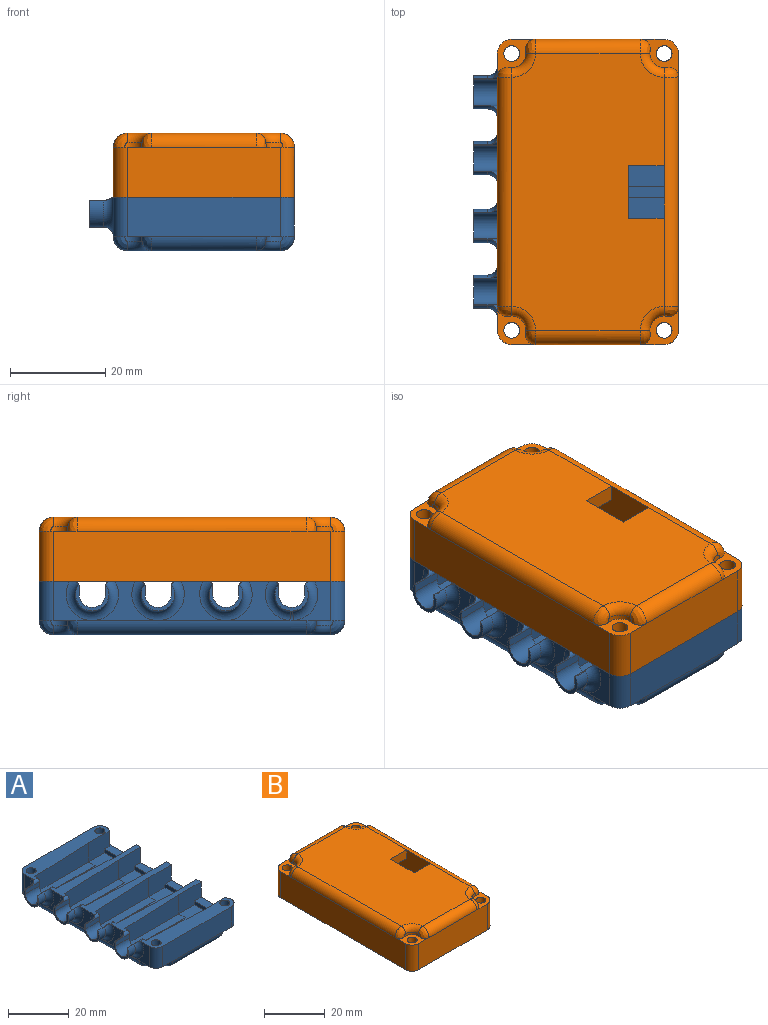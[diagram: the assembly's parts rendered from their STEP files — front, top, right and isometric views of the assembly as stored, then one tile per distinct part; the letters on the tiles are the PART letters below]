
ASSEMBLY  parts=2 mates=1
PART A: 134 faces, bbox 43.1x64.2x13.3 mm
  f0: plane 58.07x32mm, normal (0,0,-1), area 1779.6mm2, adj f87,f88,f89,f90,f123,f126,f129,f132
  f1: plane 8.2x7.75mm, normal (-1,0,0), area 28.5mm2, adj f85,f87,f99,f112,f121
  f2: plane 41.47x8.2mm, normal (-1,0,0), area 115.3mm2, adj f87,f101,f102,f103,f104,f118,f119,f120
  f3: plane 8.2x8.11mm, normal (-1,0,0), area 28.5mm2, adj f84,f87,f104,f110,f117
  f4: cylinder r=2.75mm len=6.5mm, axis (1,0,0), area 56.2mm2, adj f5,f21,f22,f98
  f5: plane 9.77x7.7mm, normal (1,0,0), area 48.1mm2, adj f4,f6,f13,f14,f21,f22,f81,f82
  f6: plane 33.5x11.85mm, normal (0,0,1), area 219.8mm2, adj f5,f7,f8,f11,f13,f14,f15,f16
  f7: plane 9.55x7.7mm, normal (0,1,0), area 70.5mm2, adj f6,f11,f12,f13,f86,f121
  f8: plane 10.5x7.7mm, normal (0,-1,0), area 76.3mm2, adj f6,f9,f11,f12,f14,f120
  f9: plane 58.07x8.2mm, normal (1,0,0), area 155.2mm2, adj f8,f12,f26,f27,f29,f44,f47,f61
  f10: plane 32x8.2mm, normal (0,-1,0), area 262.4mm2, adj f85,f86,f88,f108,f112,f121
  f11: plane 11.85x1.5mm, normal (-1,0,0), area 17.8mm2, adj f6,f7,f8,f12
  f12: plane 14.03x3mm, normal (0,0,1), area 36.2mm2, adj f7,f8,f9,f11,f86
  f13: plane 26x7.7mm, normal (0.04,1,0), area 187.9mm2, adj f5,f6,f7,f18,f19,f121
  f14: plane 26x7.7mm, normal (0.04,-1,0), area 187.9mm2, adj f5,f6,f8,f15,f16,f120
  f15: plane 25.12x4mm, normal (0.04,0,1), area 75.1mm2, adj f6,f14,f16,f17
  f16: plane 3x1mm, normal (-1,-0.04,0), area 3mm2, adj f6,f14,f15,f17
  f17: plane 25x1mm, normal (0.04,-1,0), area 12.5mm2, adj f6,f15,f16
  f18: plane 25.12x4mm, normal (0.04,0,1), area 75.1mm2, adj f6,f13,f19,f20
  f19: plane 3x1mm, normal (-1,0.04,0), area 3mm2, adj f6,f13,f18,f20
  f20: plane 25x1mm, normal (0.04,1,0), area 12.5mm2, adj f6,f18,f19
  f21: plane 6.5x1.72mm, normal (0,1,0), area 11.2mm2, adj f4,f5,f82,f98
  f22: plane 6.5x1.69mm, normal (0,-1,0), area 11mm2, adj f4,f5,f81,f98
  f23: cylinder r=2.75mm len=6.5mm, axis (1,0,0), area 56.2mm2, adj f24,f38,f39,f96
  f24: plane 9.77x7.7mm, normal (1,0,0), area 48.1mm2, adj f23,f25,f30,f31,f38,f39,f79,f80
  f25: plane 33.5x11.85mm, normal (0,0,1), area 219.8mm2, adj f24,f26,f27,f28,f30,f31,f32,f33
  f26: plane 10.5x7.7mm, normal (0,-1,0), area 76.3mm2, adj f9,f25,f28,f29,f30,f119
  f27: plane 10.5x7.7mm, normal (0,1,0), area 76.3mm2, adj f9,f25,f28,f29,f31,f120
  f28: plane 11.85x1.5mm, normal (-1,0,0), area 17.8mm2, adj f25,f26,f27,f29
  f29: plane 11.85x3mm, normal (0,0,1), area 35.6mm2, adj f9,f26,f27,f28
  f30: plane 26x7.7mm, normal (0.04,-1,0), area 187.9mm2, adj f24,f25,f26,f35,f36,f119
  f31: plane 26x7.7mm, normal (0.04,1,0), area 187.9mm2, adj f24,f25,f27,f32,f33,f120
  f32: plane 25.12x4mm, normal (0.04,0,1), area 75.1mm2, adj f25,f31,f33,f34
  f33: plane 3x1mm, normal (-1,0.04,0), area 3mm2, adj f25,f31,f32,f34
  f34: plane 25x1mm, normal (0.04,1,0), area 12.5mm2, adj f25,f32,f33
  f35: plane 25.12x4mm, normal (0.04,0,1), area 75.1mm2, adj f25,f30,f36,f37
  f36: plane 3x1mm, normal (-1,-0.04,0), area 3mm2, adj f25,f30,f35,f37
  f37: plane 25x1mm, normal (0.04,-1,0), area 12.5mm2, adj f25,f35,f36
  f38: plane 6.5x1.72mm, normal (0,-1,0), area 11.2mm2, adj f23,f24,f79,f96
  f39: plane 6.5x1.69mm, normal (0,1,0), area 11mm2, adj f23,f24,f80,f96
  f40: cylinder r=2.75mm len=6.5mm, axis (1,0,0), area 56.2mm2, adj f41,f56,f57,f92
  f41: plane 9.77x7.7mm, normal (1,0,0), area 48.1mm2, adj f40,f42,f48,f49,f56,f57,f76,f78
  f42: plane 33.5x11.85mm, normal (0,0,1), area 219.8mm2, adj f41,f43,f44,f46,f48,f49,f50,f51
  f43: plane 9.55x7.7mm, normal (0,-1,0), area 70.5mm2, adj f42,f46,f47,f48,f83,f117
  f44: plane 10.5x7.7mm, normal (0,1,0), area 76.3mm2, adj f9,f42,f46,f47,f49,f118
  f45: plane 32x8.2mm, normal (0,1,0), area 262.4mm2, adj f83,f84,f89,f106,f110,f117
  f46: plane 11.85x1.5mm, normal (-1,0,0), area 17.8mm2, adj f42,f43,f44,f47
  f47: plane 14.03x3mm, normal (0,0,1), area 36.2mm2, adj f9,f43,f44,f46,f83
  f48: plane 26x7.7mm, normal (0.04,-1,0), area 187.9mm2, adj f41,f42,f43,f53,f54,f117
  f49: plane 26x7.7mm, normal (0.04,1,0), area 187.9mm2, adj f41,f42,f44,f50,f51,f118
  f50: plane 25.12x4mm, normal (0.04,0,1), area 75.1mm2, adj f42,f49,f51,f52
  f51: plane 3x1mm, normal (-1,0.04,0), area 3mm2, adj f42,f49,f50,f52
  f52: plane 25x1mm, normal (0.04,1,0), area 12.5mm2, adj f42,f50,f51
  f53: plane 25.12x4mm, normal (0.04,0,1), area 75.1mm2, adj f42,f48,f54,f55
  f54: plane 3x1mm, normal (-1,-0.04,0), area 3mm2, adj f42,f48,f53,f55
  f55: plane 25x1mm, normal (0.04,-1,0), area 12.5mm2, adj f42,f53,f54
  f56: plane 6.5x1.72mm, normal (0,-1,0), area 11.2mm2, adj f40,f41,f76,f92
  f57: plane 6.5x1.69mm, normal (0,1,0), area 11mm2, adj f40,f41,f78,f92
  f58: cylinder r=2.75mm len=6.5mm, axis (1,0,0), area 56.2mm2, adj f59,f73,f74,f94
  f59: plane 9.77x7.7mm, normal (1,0,0), area 48.1mm2, adj f58,f60,f65,f66,f73,f74,f75,f77
  f60: plane 33.5x11.85mm, normal (0,0,1), area 219.8mm2, adj f59,f61,f62,f63,f65,f66,f67,f68
  f61: plane 10.5x7.7mm, normal (0,1,0), area 76.3mm2, adj f9,f60,f63,f64,f65,f119
  f62: plane 10.5x7.7mm, normal (0,-1,0), area 76.3mm2, adj f9,f60,f63,f64,f66,f118
  f63: plane 11.85x1.5mm, normal (-1,0,0), area 17.8mm2, adj f60,f61,f62,f64
  f64: plane 11.85x3mm, normal (0,0,1), area 35.6mm2, adj f9,f61,f62,f63
  f65: plane 26x7.7mm, normal (0.04,1,0), area 187.9mm2, adj f59,f60,f61,f70,f71,f119
  f66: plane 26x7.7mm, normal (0.04,-1,0), area 187.9mm2, adj f59,f60,f62,f67,f68,f118
  f67: plane 25.12x4mm, normal (0.04,0,1), area 75.1mm2, adj f60,f66,f68,f69
  f68: plane 3x1mm, normal (-1,-0.04,0), area 3mm2, adj f60,f66,f67,f69
  f69: plane 25x1mm, normal (0.04,-1,0), area 12.5mm2, adj f60,f67,f68
  f70: plane 25.12x4mm, normal (0.04,0,1), area 75.1mm2, adj f60,f65,f71,f72
  f71: plane 3x1mm, normal (-1,0.04,0), area 3mm2, adj f60,f65,f70,f72
  f72: plane 25x1mm, normal (0.04,1,0), area 12.5mm2, adj f60,f70,f71
  f73: plane 6.5x1.72mm, normal (0,1,0), area 11.2mm2, adj f58,f59,f75,f94
  f74: plane 6.5x1.69mm, normal (0,-1,0), area 11mm2, adj f58,f59,f77,f94
  f75: cylinder r=1mm len=6.5mm, axis (1,0,0), area 5mm2, adj f59,f73,f93,f94,f103,f119
  f76: cylinder r=1mm len=6.5mm, axis (1,0,0), area 5mm2, adj f41,f56,f91,f92,f104,f117
  f77: cylinder r=1mm len=6.5mm, axis (-1,0,0), area 5.2mm2, adj f59,f74,f93,f94,f103,f118
  f78: cylinder r=1mm len=6.5mm, axis (-1,0,0), area 5.1mm2, adj f41,f57,f91,f92,f104,f118
  f79: cylinder r=1mm len=6.5mm, axis (1,0,0), area 5mm2, adj f24,f38,f95,f96,f102,f119
  f80: cylinder r=1mm len=6.5mm, axis (-1,0,0), area 5.2mm2, adj f24,f39,f95,f96,f102,f120
  f81: cylinder r=1mm len=6.5mm, axis (-1,0,0), area 5.1mm2, adj f5,f22,f97,f98,f101,f120
  f82: cylinder r=1mm len=6.5mm, axis (1,0,0), area 4.9mm2, adj f5,f21,f97,f98,f99,f121
  f83: cylinder r=3mm len=8.2mm, axis (0,0,-1), area 53.8mm2, adj f9,f43,f45,f47,f106,f117
  f84: cylinder r=3mm len=8.2mm, axis (0,0,-1), area 38.6mm2, adj f3,f45,f110,f117
  f85: cylinder r=3mm len=8.2mm, axis (0,0,-1), area 38.6mm2, adj f1,f10,f112,f121
  f86: cylinder r=3mm len=8.2mm, axis (0,0,-1), area 53.8mm2, adj f7,f9,f10,f12,f108,f121
  f87: cylinder r=3mm len=48.27mm, axis (0,-1,0), area 227mm2, adj f0,f1,f2,f3,f100,f124,f125
  f88: cylinder r=3mm len=22.2mm, axis (1,0,0), area 104.1mm2, adj f0,f10,f122,f128
  f89: cylinder r=3mm len=22.2mm, axis (1,0,0), area 104.1mm2, adj f0,f45,f127,f133
  f90: cylinder r=3mm len=48.27mm, axis (0,1,0), area 227mm2, adj f0,f9,f130,f131
  f91: cylinder r=3.5mm len=7mm, axis (1,0,0), area 46.3mm2, adj f76,f78,f92,f104
  f92: plane 7x5.57mm, normal (-1,0,0), area 9.5mm2, adj f40,f56,f57,f76,f78,f91
  f93: cylinder r=3.5mm len=7mm, axis (1,0,0), area 46.2mm2, adj f75,f77,f94,f103
  f94: plane 7x5.58mm, normal (-1,0,0), area 9.5mm2, adj f58,f73,f74,f75,f77,f93
  f95: cylinder r=3.5mm len=7mm, axis (1,0,0), area 46.2mm2, adj f79,f80,f96,f102
  f96: plane 7x5.58mm, normal (-1,0,0), area 9.5mm2, adj f23,f38,f39,f79,f80,f95
  f97: cylinder r=3.5mm len=7mm, axis (1,0,0), area 46.3mm2, adj f81,f82,f98,f99,f100,f101
  f98: plane 7x5.59mm, normal (-1,0,0), area 9.6mm2, adj f4,f21,f22,f81,f82,f97
  f99: torus R=5.5mm, axis (-1,0,0), area 28.2mm2, adj f1,f82,f97,f100,f121
  f100: bspline ~3.15x2.14mm, area 1.8mm2, adj f87,f97,f99,f101
  f101: torus R=5.5mm, axis (-1,0,0), area 28.3mm2, adj f2,f81,f97,f100,f120
  f102: torus R=5.5mm, axis (-1,0,0), area 58.2mm2, adj f2,f79,f80,f95,f119,f120
  f103: torus R=5.5mm, axis (-1,0,0), area 58.2mm2, adj f2,f75,f77,f93,f118,f119
  f104: torus R=5.5mm, axis (-1,0,0), area 58.3mm2, adj f2,f3,f76,f78,f91,f117,f118
  f105: cylinder r=3mm len=3.6mm, axis (0,0,-1), area 5.7mm2, adj f106,f131,f132,f133
  f106: plane 7.99x7.99mm, normal (0,0,-1), area 24.8mm2, adj f9,f45,f83,f105,f116,f131,f133
  f107: cylinder r=3mm len=3.6mm, axis (0,0,-1), area 5.7mm2, adj f108,f128,f129,f130
  f108: plane 7.99x7.99mm, normal (0,0,-1), area 24.8mm2, adj f9,f10,f86,f107,f114,f128,f130
  f109: cylinder r=3mm len=3.6mm, axis (0,0,-1), area 5.7mm2, adj f110,f125,f126,f127
  f110: plane 7.99x7.99mm, normal (0,0,-1), area 24.8mm2, adj f3,f45,f84,f109,f115,f125,f127
  f111: cylinder r=3mm len=3.6mm, axis (0,0,-1), area 5.7mm2, adj f112,f122,f123,f124
  f112: plane 7.99x7.99mm, normal (0,0,-1), area 24.8mm2, adj f1,f10,f85,f111,f113,f122,f124
  f113: cylinder r=1.65mm len=8.2mm, axis (0,0,-1), area 85mm2, adj f112,f121
  f114: cylinder r=1.65mm len=8.2mm, axis (0,0,-1), area 85mm2, adj f108,f121
  f115: cylinder r=1.65mm len=8.2mm, axis (0,0,-1), area 85mm2, adj f110,f117
  f116: cylinder r=1.65mm len=8.2mm, axis (0,0,-1), area 85mm2, adj f106,f117
  f117: plane 38.24x7.39mm, normal (0,0,1), area 192.2mm2, adj f3,f41,f43,f45,f48,f76,f83,f84
  f118: plane 38.25x6.36mm, normal (0,0,1), area 108.5mm2, adj f2,f9,f41,f44,f49,f59,f62,f66
  f119: plane 38.24x6.74mm, normal (0,0,1), area 123.6mm2, adj f2,f9,f24,f26,f30,f59,f61,f65
  f120: plane 38.25x6.36mm, normal (0,0,1), area 108.5mm2, adj f2,f5,f8,f9,f14,f24,f27,f31
  f121: plane 38.23x7.39mm, normal (0,0,1), area 192.2mm2, adj f1,f5,f7,f10,f13,f82,f85,f86
  f122: bspline ~3.56x3.51mm, area 11.5mm2, adj f88,f111,f112,f123
  f123: torus R=5mm, axis (0,0,1), area 18.4mm2, adj f0,f111,f122,f124
  f124: bspline ~3.56x3.51mm, area 11.5mm2, adj f87,f111,f112,f123
  f125: bspline ~3.56x3.51mm, area 11.5mm2, adj f87,f109,f110,f126
  f126: torus R=5mm, axis (0,0,1), area 18.4mm2, adj f0,f109,f125,f127
  f127: bspline ~3.56x3.51mm, area 11.5mm2, adj f89,f109,f110,f126
  f128: bspline ~3.56x3.51mm, area 11.5mm2, adj f88,f107,f108,f129
  f129: torus R=5mm, axis (0,0,1), area 18.4mm2, adj f0,f107,f128,f130
  f130: bspline ~3.56x3.51mm, area 11.5mm2, adj f90,f107,f108,f129
  f131: bspline ~3.56x3.51mm, area 11.5mm2, adj f90,f105,f106,f132
  f132: torus R=5mm, axis (0,0,1), area 18.4mm2, adj f0,f105,f131,f133
  f133: bspline ~3.56x3.51mm, area 11.5mm2, adj f89,f105,f106,f132
PART B: 115 faces, bbox 38.1x64.2x13.6 mm
  f0: plane 21.35x7.51mm, normal (0,0,-1), area 160.4mm2, adj f5,f62,f79,f113
  f1: plane 58.07x32mm, normal (0,0,1), area 1697.2mm2, adj f2,f35,f36,f47,f79,f86,f89,f96
  f2: cylinder r=3mm len=48.27mm, axis (0,1,0), area 226.8mm2, adj f1,f4,f5,f85,f98,f113,f114
  f3: plane 3.93x2.98mm, normal (0,0,-1), area 11.7mm2, adj f4,f5,f23,f110
  f4: plane 58.07x10.5mm, normal (1,0,0), area 503.8mm2, adj f2,f3,f6,f7,f8,f14,f15,f16
  f5: plane 53.7x13.5mm, normal (-1,0,0), area 471.8mm2, adj f0,f2,f3,f6,f7,f8,f14,f15
  f6: plane 3.93x2.98mm, normal (0,0,-1), area 11.7mm2, adj f4,f5,f21,f107
  f7: plane 3.93x2.98mm, normal (0,0,-1), area 11.7mm2, adj f4,f5,f20,f104
  f8: plane 6.11x2.98mm, normal (0,0,-1), area 12.3mm2, adj f4,f5,f59,f62,f101
  f9: cylinder r=3mm len=10.5mm, axis (0,0,-1), area 49.5mm2, adj f60,f77,f78,f91
  f10: cylinder r=1.65mm len=10.5mm, axis (0,0,-1), area 108.9mm2, adj f78,f93
  f11: cylinder r=1.65mm len=10.5mm, axis (0,0,-1), area 108.9mm2, adj f78,f91
  f12: cylinder r=1.65mm len=10.5mm, axis (0,0,-1), area 108.9mm2, adj f78,f83
  f13: cylinder r=1.65mm len=10.5mm, axis (0,0,-1), area 108.9mm2, adj f78,f81
  f14: plane 3.93x2.98mm, normal (0,0,-1), area 11.7mm2, adj f4,f5,f19,f105
  f15: plane 3.93x2.98mm, normal (0,0,-1), area 11.7mm2, adj f4,f5,f22,f108
  f16: plane 6.11x2.98mm, normal (0,0,-1), area 12.3mm2, adj f4,f5,f72,f74,f111
  f17: plane 3.93x2.98mm, normal (0,0,-1), area 11.7mm2, adj f4,f5,f18,f102
  f18: plane 2.98x0.5mm, normal (0,-1,0), area 1.5mm2, adj f4,f5,f17,f24
  f19: plane 2.98x0.5mm, normal (0,-1,0), area 1.5mm2, adj f4,f5,f14,f25
  f20: plane 2.98x0.5mm, normal (0,1,0), area 1.5mm2, adj f4,f5,f7,f24
  f21: plane 2.98x0.5mm, normal (0,-1,0), area 1.5mm2, adj f4,f5,f6,f26
  f22: plane 2.98x0.5mm, normal (0,1,0), area 1.5mm2, adj f4,f5,f15,f25
  f23: plane 2.98x0.5mm, normal (0,1,0), area 1.5mm2, adj f3,f4,f5,f26
  f24: plane 2.98x1.97mm, normal (0,0,-1), area 5.9mm2, adj f4,f5,f18,f20
  f25: plane 2.98x2.37mm, normal (0,0,-1), area 7.1mm2, adj f4,f5,f19,f22
  f26: plane 2.98x1.97mm, normal (0,0,-1), area 5.9mm2, adj f4,f5,f21,f23
  f27: plane 24.88x1mm, normal (0.04,1,0), area 12.5mm2, adj f37,f38,f39,f79
  f28: plane 24.88x1mm, normal (0.04,-1,0), area 12.5mm2, adj f39,f40,f41,f79
  f29: plane 24.88x1mm, normal (0.04,1,0), area 12.5mm2, adj f44,f45,f46,f79
  f30: plane 24.88x1mm, normal (0.04,-1,0), area 12.5mm2, adj f42,f43,f46,f79
  f31: plane 24.88x1mm, normal (0.04,1,0), area 12.5mm2, adj f50,f51,f52,f79
  f32: plane 24.88x1mm, normal (0.04,-1,0), area 12.5mm2, adj f48,f49,f52,f79
  f33: plane 24.88x1mm, normal (0.04,1,0), area 12.5mm2, adj f53,f54,f55,f79
  f34: plane 24.88x1mm, normal (0.04,-1,0), area 12.5mm2, adj f55,f56,f57,f79
  f35: cylinder r=3mm len=48.27mm, axis (0,-1,0), area 227mm2, adj f1,f77,f90,f95
  f36: cylinder r=3mm len=22.2mm, axis (1,0,0), area 104.1mm2, adj f1,f60,f97,f100
  f37: plane 25x4mm, normal (0.04,0,-1), area 74.9mm2, adj f27,f38,f61,f79
  f38: plane 3x1mm, normal (-1,0.04,0), area 3mm2, adj f27,f37,f39,f61
  f39: plane 26x9.85mm, normal (0,0,-1), area 131.3mm2, adj f27,f28,f38,f40,f58,f61,f63,f79
  f40: plane 3x1mm, normal (-1,-0.04,0), area 3mm2, adj f28,f39,f41,f58
  f41: plane 25x4mm, normal (0.04,0,-1), area 74.9mm2, adj f28,f40,f58,f79
  f42: plane 3x1mm, normal (-1,-0.04,0), area 3mm2, adj f30,f43,f46,f64
  f43: plane 25x4mm, normal (0.04,0,-1), area 74.9mm2, adj f30,f42,f64,f79
  f44: plane 25x4mm, normal (0.04,0,-1), area 74.9mm2, adj f29,f45,f65,f79
  f45: plane 3x1mm, normal (-1,0.04,0), area 3mm2, adj f29,f44,f46,f65
  f46: plane 26x9.85mm, normal (0,0,-1), area 131.3mm2, adj f29,f30,f42,f45,f64,f65,f66,f79
  f47: cylinder r=3mm len=22.2mm, axis (1,0,0), area 104.1mm2, adj f1,f73,f87,f88
  f48: plane 3x1mm, normal (-1,-0.04,0), area 3mm2, adj f32,f49,f52,f70
  f49: plane 25x4mm, normal (0.04,0,-1), area 74.9mm2, adj f32,f48,f70,f79
  f50: plane 25x4mm, normal (0.04,0,-1), area 74.9mm2, adj f31,f51,f75,f79
  f51: plane 3x1mm, normal (-1,0.04,0), area 3mm2, adj f31,f50,f52,f75
  f52: plane 26x9.85mm, normal (0,0,-1), area 131.3mm2, adj f31,f32,f48,f51,f70,f75,f76,f79
  f53: plane 25x4mm, normal (0.04,0,-1), area 74.9mm2, adj f33,f54,f68,f79
  f54: plane 3x1mm, normal (-1,0.04,0), area 3mm2, adj f33,f53,f55,f68
  f55: plane 26x9.85mm, normal (0,0,-1), area 131.3mm2, adj f33,f34,f54,f56,f67,f68,f69,f79
  f56: plane 3x1mm, normal (-1,-0.04,0), area 3mm2, adj f34,f55,f57,f67
  f57: plane 25x4mm, normal (0.04,0,-1), area 74.9mm2, adj f34,f56,f67,f79
  f58: plane 26x2mm, normal (0.04,-1,0), area 39.5mm2, adj f39,f40,f41,f63,f78,f79
  f59: cylinder r=3mm len=10.5mm, axis (0,0,-1), area 50.7mm2, adj f4,f8,f60,f62,f78,f93
  f60: plane 32x10.5mm, normal (0,-1,0), area 336mm2, adj f9,f36,f59,f78,f91,f93
  f61: plane 26x2mm, normal (0.04,1,0), area 39.5mm2, adj f37,f38,f39,f62,f63,f78
  f62: plane 10x9.55mm, normal (0,1,0), area 76.2mm2, adj f0,f5,f8,f59,f61,f78,f79
  f63: plane 9.77x2mm, normal (1,0,0), area 19.5mm2, adj f39,f58,f61,f78
  f64: plane 26x2mm, normal (0.04,-1,0), area 39.5mm2, adj f42,f43,f46,f66,f78,f79
  f65: plane 26x2mm, normal (0.04,1,0), area 39.5mm2, adj f44,f45,f46,f66,f78,f79
  f66: plane 9.77x2mm, normal (1,0,0), area 19.5mm2, adj f46,f64,f65,f78
  f67: plane 26x2mm, normal (0.04,-1,0), area 39.5mm2, adj f55,f56,f57,f69,f78,f79
  f68: plane 26x2mm, normal (0.04,1,0), area 39.5mm2, adj f53,f54,f55,f69,f78,f79
  f69: plane 9.77x2mm, normal (1,0,0), area 19.5mm2, adj f55,f67,f68,f78
  f70: plane 26x2mm, normal (0.04,-1,0), area 39.5mm2, adj f48,f49,f52,f74,f76,f78
  f71: cylinder r=3mm len=10.5mm, axis (0,0,-1), area 49.5mm2, adj f73,f77,f78,f81
  f72: cylinder r=3mm len=10.5mm, axis (0,0,-1), area 50.7mm2, adj f4,f16,f73,f74,f78,f83
  f73: plane 32x10.5mm, normal (0,1,0), area 336mm2, adj f47,f71,f72,f78,f81,f83
  f74: plane 10x9.55mm, normal (0,-1,0), area 76.2mm2, adj f5,f16,f70,f72,f78,f79,f80
  f75: plane 26x2mm, normal (0.04,1,0), area 39.5mm2, adj f50,f51,f52,f76,f78,f79
  f76: plane 9.77x2mm, normal (1,0,0), area 19.5mm2, adj f52,f70,f75,f78
  f77: plane 58.08x10.52mm, normal (-1,0,0), area 609.7mm2, adj f9,f35,f71,f78,f81,f91
  f78: plane 64.07x38mm, normal (0,0,-1), area 703.3mm2, adj f9,f10,f11,f12,f13,f58,f59,f60
  f79: plane 53.7x13.5mm, normal (1,0,0), area 480.8mm2, adj f0,f1,f27,f28,f29,f30,f31,f32
  f80: plane 21.35x7.51mm, normal (0,0,-1), area 160.4mm2, adj f5,f74,f79,f114
  f81: plane 7.99x7.99mm, normal (0,0,1), area 24.8mm2, adj f13,f71,f73,f77,f82,f88,f90
  f82: cylinder r=3mm len=3.6mm, axis (0,0,1), area 5.7mm2, adj f81,f88,f89,f90
  f83: plane 7.99x7.99mm, normal (0,0,1), area 24.8mm2, adj f4,f12,f72,f73,f84,f85,f87
  f84: cylinder r=3mm len=3.6mm, axis (0,0,1), area 5.7mm2, adj f83,f85,f86,f87
  f85: bspline ~3.56x3.51mm, area 11.5mm2, adj f2,f83,f84,f86
  f86: torus R=5mm, axis (0,0,-1), area 18.4mm2, adj f1,f84,f85,f87
  f87: bspline ~3.56x3.51mm, area 11.5mm2, adj f47,f83,f84,f86
  f88: bspline ~3.56x3.51mm, area 11.5mm2, adj f47,f81,f82,f89
  f89: torus R=5mm, axis (0,0,-1), area 18.4mm2, adj f1,f82,f88,f90
  f90: bspline ~3.56x3.51mm, area 11.5mm2, adj f35,f81,f82,f89
  f91: plane 7.99x7.99mm, normal (0,0,1), area 24.8mm2, adj f9,f11,f60,f77,f92,f95,f97
  f92: cylinder r=3mm len=3.6mm, axis (0,0,1), area 5.7mm2, adj f91,f95,f96,f97
  f93: plane 7.99x7.99mm, normal (0,0,1), area 24.8mm2, adj f4,f10,f59,f60,f94,f98,f100
  f94: cylinder r=3mm len=3.6mm, axis (0,0,1), area 5.7mm2, adj f93,f98,f99,f100
  f95: bspline ~3.56x3.51mm, area 11.5mm2, adj f35,f91,f92,f96
  f96: torus R=5mm, axis (0,0,-1), area 18.4mm2, adj f1,f92,f95,f97
  f97: bspline ~3.56x3.51mm, area 11.5mm2, adj f36,f91,f92,f96
  f98: bspline ~3.56x3.51mm, area 11.5mm2, adj f2,f93,f94,f99
  f99: torus R=5mm, axis (0,0,-1), area 18.4mm2, adj f1,f94,f98,f100
  f100: bspline ~3.56x3.51mm, area 11.5mm2, adj f36,f93,f94,f99
  f101: plane 5x2.98mm, normal (0,1,0), area 14.9mm2, adj f4,f5,f8,f103
  f102: plane 5x2.98mm, normal (0,-1,0), area 14.9mm2, adj f4,f5,f17,f103
  f103: plane 4x2.98mm, normal (0,0,-1), area 11.9mm2, adj f4,f5,f101,f102
  f104: plane 5x2.98mm, normal (0,1,0), area 14.9mm2, adj f4,f5,f7,f106
  f105: plane 5x2.98mm, normal (0,-1,0), area 14.9mm2, adj f4,f5,f14,f106
  f106: plane 4x2.98mm, normal (0,0,-1), area 11.9mm2, adj f4,f5,f104,f105
  f107: plane 5x2.98mm, normal (0,-1,0), area 14.9mm2, adj f4,f5,f6,f109
  f108: plane 5x2.98mm, normal (0,1,0), area 14.9mm2, adj f4,f5,f15,f109
  f109: plane 4x2.98mm, normal (0,0,-1), area 11.9mm2, adj f4,f5,f107,f108
  f110: plane 5x2.98mm, normal (0,1,0), area 14.9mm2, adj f3,f4,f5,f112
  f111: plane 5x2.98mm, normal (0,-1,0), area 14.9mm2, adj f4,f5,f16,f112
  f112: plane 4x2.98mm, normal (0,0,-1), area 11.9mm2, adj f4,f5,f110,f111
  f113: plane 7.51x3.5mm, normal (0,1,0), area 26.3mm2, adj f0,f1,f2,f5,f79
  f114: plane 7.51x3.5mm, normal (0,-1,0), area 26.3mm2, adj f1,f2,f5,f79,f80
PLACE A t=(-73.97,-1.7,108.52)mm
PLACE B t=(-73.97,-1.7,102.83)mm
MATE fastened B.f12 <-> A.f83  axis (0,0,-1) through (-66.47,48.66,117.72)mm
